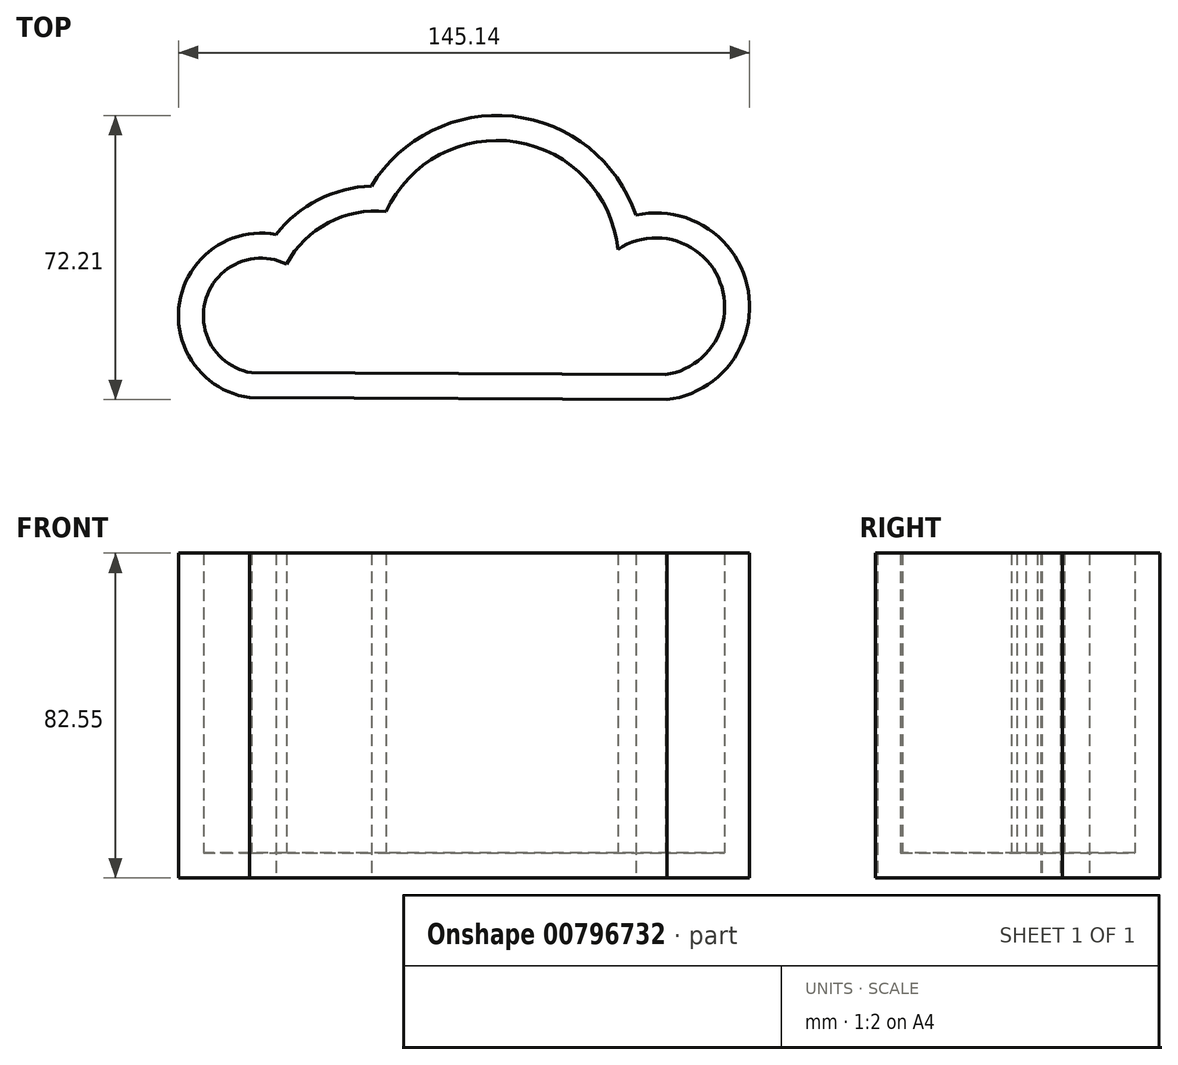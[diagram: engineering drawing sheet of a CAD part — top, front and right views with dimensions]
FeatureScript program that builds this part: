
annotation { "Feature Type Name" : "Feature", "Feature Type Description" : "" }
export const myFeature = defineFeature(function(context is Context, id is Id, definition is map)
    precondition{}
    {
        {
            var Q0;
            Q0=qCreatedBy(makeId("Top.planeOp"),FACE);
            var sketch = newSketch(context, id + "F0", { "sketchPlane" : qUnion([Q0])});
            skArc(sketch, "E0", {"start": v(-23.63, 18.02) * mm, "mid": v(-37.12, 14.56) * mm, "end": v(-47.87, 5.72) * mm});
            skArc(sketch, "E1", {"start": v(43.57, 10.65) * mm, "mid": v(12.32, 35.75) * mm, "end": v(-23.63, 18.02) * mm});
            skArc(sketch, "E2", {"start": v(51.43, -36.24) * mm, "mid": v(72.14, -8.67) * mm, "end": v(43.57, 10.65) * mm});
            skArc(sketch, "E3", {"start": v(-47.87, 5.72) * mm, "mid": v(-72.4, -11.57) * mm, "end": v(-54.6, -35.74) * mm});
            skLineSegment(sketch, "E4", {"start": v(-54.6, -35.74) * mm, "end": v(51.43, -36.24) * mm});
            skSolve(sketch);
        }
        {
            var Q0;
            Q0 = qSketchRegion(id + "F0", true);
            extrude(context, id + "F1", {"entities" : qUnion([Q0]), "depth" : 6.35 * mm, "offsetDistance" : 25.4 * mm});
        }
        {
            var Q0;
            Q0=makeQuery(id+"F1.opExtrude","CAP_FACE",FACE,{"disambiguationData":[OSD([sQuery(id+"F0.wireOp",EDGE,"E0"),sQuery(id+"F0.wireOp",EDGE,"E1"),sQuery(id+"F0.wireOp",EDGE,"E2"),sQuery(id+"F0.wireOp",EDGE,"E3"),sQuery(id+"F0.wireOp",EDGE,"E4")])],"isStart":false});
            var sketch = newSketch(context, id + "F2", { "sketchPlane" : qUnion([Q0])});
            skArc(sketch, "E5.0", {"start": v(-19.88, 11.54) * mm, "mid": v(-34.57, 8.73) * mm, "end": v(-45.22, -1.78) * mm});
            skArc(sketch, "E5.1", {"start": v(39.02, 1.94) * mm, "mid": v(13.23, 29.22) * mm, "end": v(-19.88, 11.54) * mm});
            skArc(sketch, "E5.2", {"start": v(-45.22, -1.78) * mm, "mid": v(-65.61, -10.45) * mm, "end": v(-54.1, -29.39) * mm});
            skLineSegment(sketch, "E5.3", {"start": v(-54.1, -29.39) * mm, "end": v(51.04, -29.89) * mm});
            skArc(sketch, "E5.4", {"start": v(51.04, -29.89) * mm, "mid": v(65, -6.43) * mm, "end": v(39.02, 1.94) * mm});
            skLineSegment(sketch, "E6.0", {"start": v(-54.6, -35.74) * mm, "end": v(51.43, -36.24) * mm});
            skArc(sketch, "E6.1", {"start": v(-47.87, 5.72) * mm, "mid": v(-72.4, -11.57) * mm, "end": v(-54.6, -35.74) * mm});
            skArc(sketch, "E6.2", {"start": v(51.43, -36.24) * mm, "mid": v(72.14, -8.67) * mm, "end": v(43.57, 10.65) * mm});
            skArc(sketch, "E6.3", {"start": v(43.57, 10.65) * mm, "mid": v(12.32, 35.75) * mm, "end": v(-23.63, 18.02) * mm});
            skArc(sketch, "E6.4", {"start": v(-23.63, 18.02) * mm, "mid": v(-37.12, 14.56) * mm, "end": v(-47.87, 5.72) * mm});
            skSolve(sketch);
        }
        {
            var Q0;
            Q0 = qSketchRegion(id + "F2", true);
            extrude(context, id + "F3", {"entities" : qUnion([Q0]), "operationType" : NewBodyOperationType.ADD, "depth" : 76.2 * mm, "offsetDistance" : 25.4 * mm});
        }
    });
